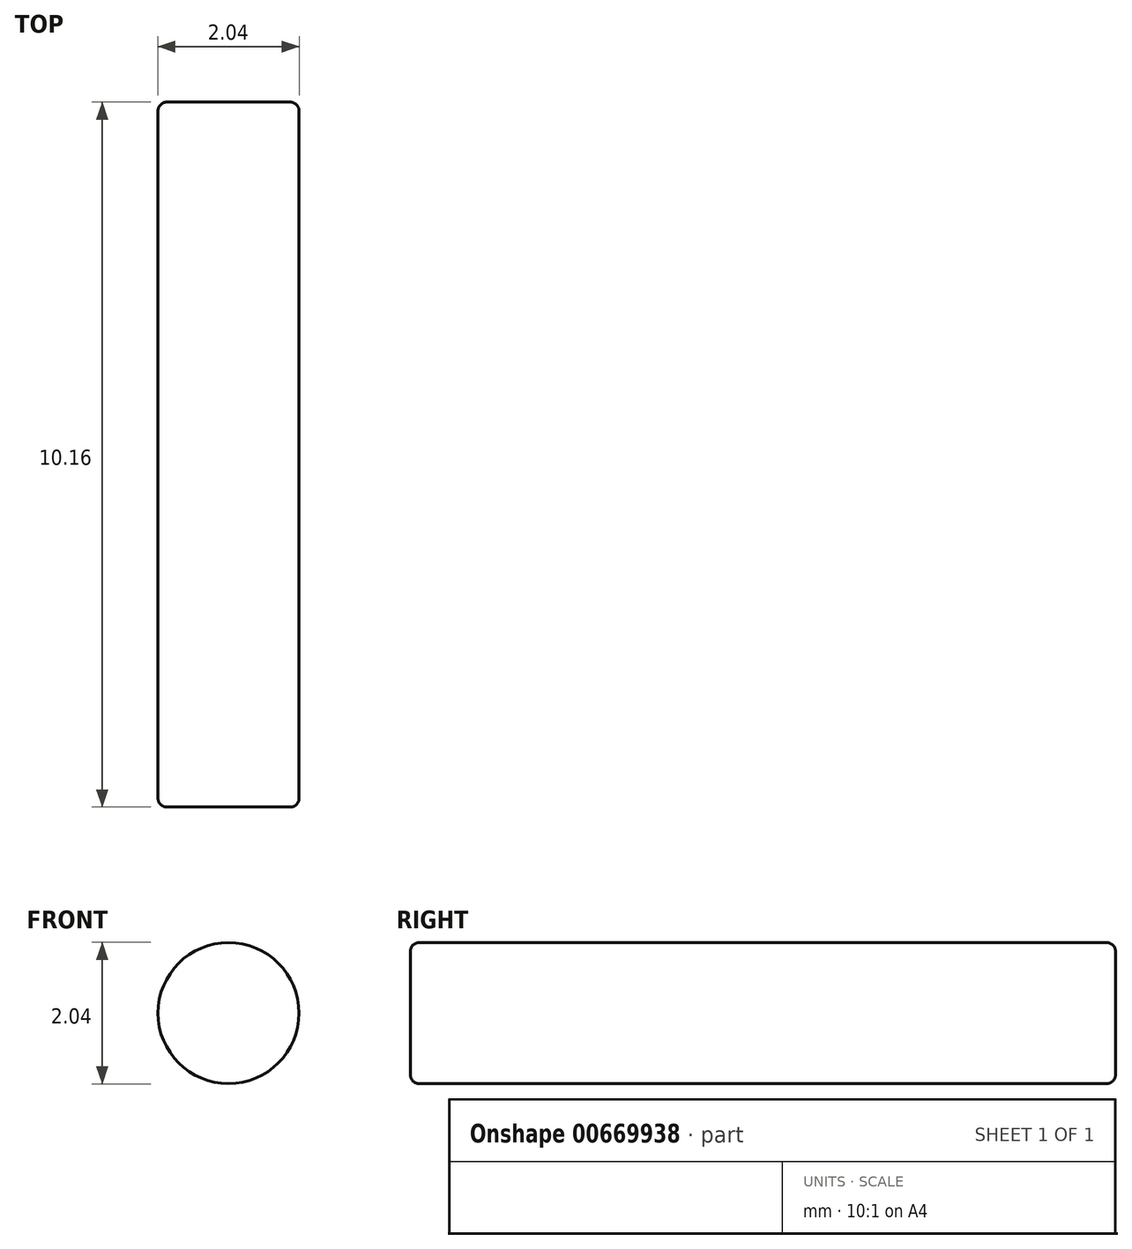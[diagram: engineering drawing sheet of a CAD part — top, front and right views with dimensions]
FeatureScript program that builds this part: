
annotation { "Feature Type Name" : "Feature", "Feature Type Description" : "" }
export const myFeature = defineFeature(function(context is Context, id is Id, definition is map)
    precondition{}
    {
        {
            var Q0;
            Q0=qCreatedBy(makeId("Front.planeOp"),FACE);
            var sketch = newSketch(context, id + "F0", { "sketchPlane" : qUnion([Q0])});
            skCircle(sketch, "E0", {"center": v(0, 0) * mm, "radius": 1.02 * mm});
            skSolve(sketch);
        }
        {
            var Q0;
            Q0=qSketchRegion(id+"F0",true);
            extrude(context, id + "F1", {"entities" : qUnion([Q0]), "endBound" : BoundingType.SYMMETRIC, "depth" : 10.16 * mm, "offsetDistance" : 25.4 * mm});
        }
        {
            var Q0;
            Q0=makeQuery(id+"F1.opExtrude","CAP_EDGE",EDGE,{"disambiguationData":[OSD([sQuery(id+"F0.wireOp",EDGE,"E0")])],"isStart":false});
            var Q1;
            Q1=makeQuery(id+"F1.opExtrude","CAP_EDGE",EDGE,{"disambiguationData":[OSD([sQuery(id+"F0.wireOp",EDGE,"E0")])],"isStart":true});
            fillet(context, id + "F2", {"entities" : qUnion([Q0, Q1]), "radius" : 0.13 * mm, "tangentPropagation" : true, "allowEdgeOverflow" : false});
        }
    });
